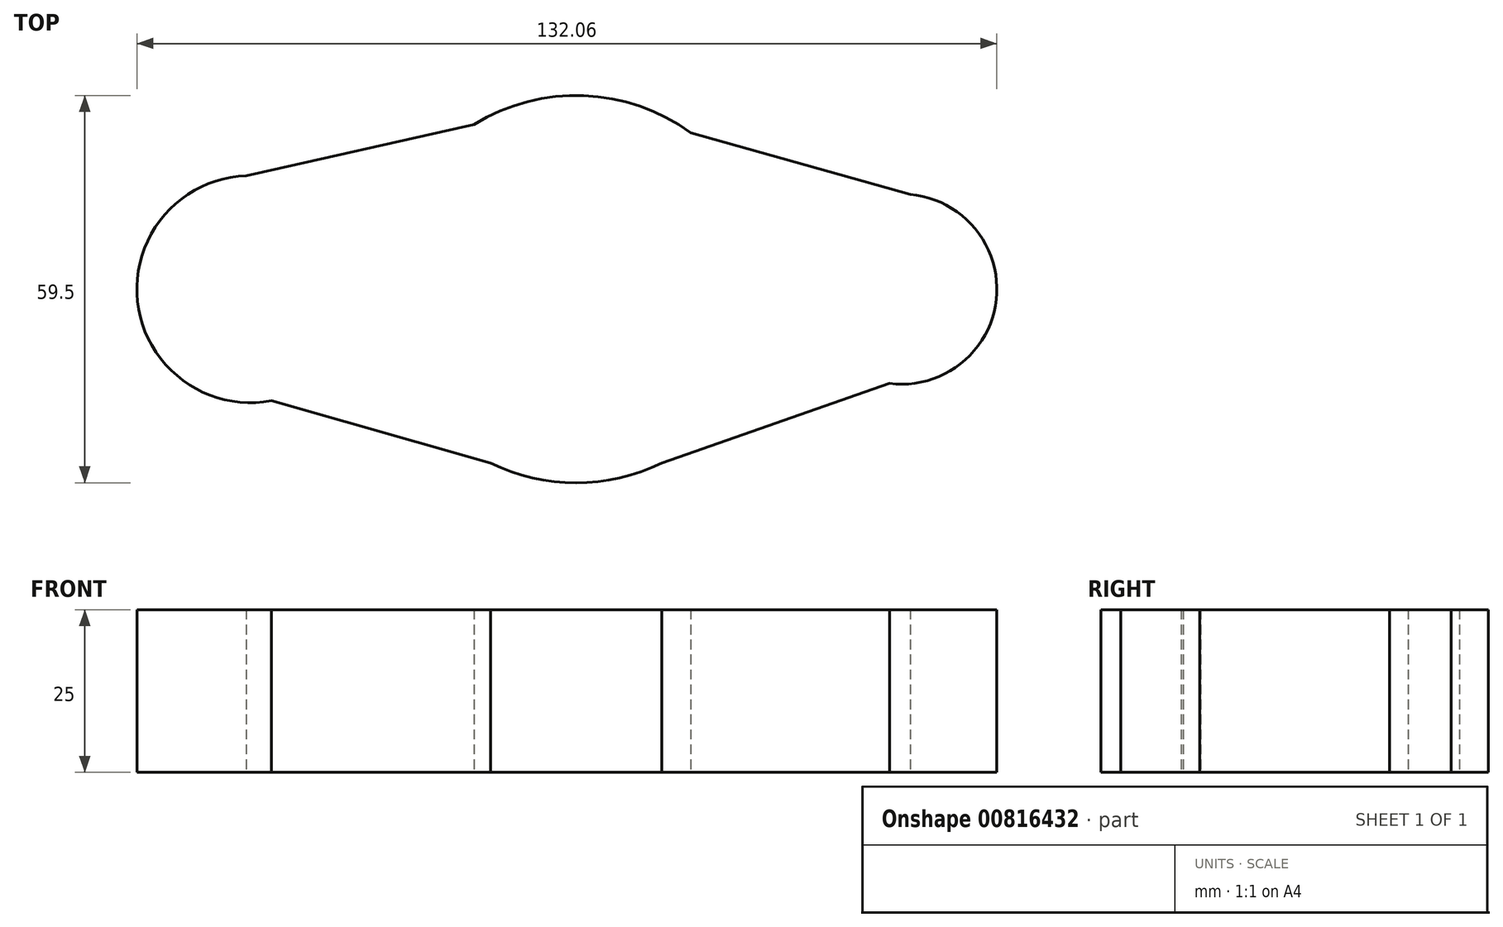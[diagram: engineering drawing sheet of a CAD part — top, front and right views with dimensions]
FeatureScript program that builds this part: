
annotation { "Feature Type Name" : "Feature", "Feature Type Description" : "" }
export const myFeature = defineFeature(function(context is Context, id is Id, definition is map)
    precondition{}
    {
        {
            var Q0;
            Q0=qCreatedBy(makeId("Top.planeOp"),FACE);
            var sketch = newSketch(context, id + "F0", { "sketchPlane" : qUnion([Q0])});
            skArc(sketch, "E0", {"start": v(-13.14, -26.7) * mm, "mid": v(0, -29.75) * mm, "end": v(13.14, -26.7) * mm});
            skArc(sketch, "E1", {"start": v(48.14, -14.49) * mm, "mid": v(64.52, -1.59) * mm, "end": v(51.31, 14.55) * mm});
            skArc(sketch, "E2", {"start": v(-50.65, 17.44) * mm, "mid": v(-67.34, -1.92) * mm, "end": v(-46.82, -17.15) * mm});
            skLineSegment(sketch, "E3", {"start": v(-46.82, -17.15) * mm, "end": v(-13.14, -26.7) * mm});
            skLineSegment(sketch, "E4", {"start": v(13.14, -26.7) * mm, "end": v(48.14, -14.49) * mm});
            skLineSegment(sketch, "E5", {"start": v(-50.65, 17.44) * mm, "end": v(-15.65, 25.3) * mm});
            skLineSegment(sketch, "E6", {"start": v(17.6, 23.98) * mm, "end": v(51.31, 14.55) * mm});
            skArc(sketch, "E7.trimOffspring", {"start": v(17.6, 23.98) * mm, "mid": v(1.18, 29.73) * mm, "end": v(-15.65, 25.3) * mm});
            skSolve(sketch);
        }
        {
            var Q0;
            Q0 = qSketchRegion(id + "F0", true);
            extrude(context, id + "F1", {"entities" : qUnion([Q0]), "depth" : 25 * mm, "offsetDistance" : 25 * mm});
        }
    });
